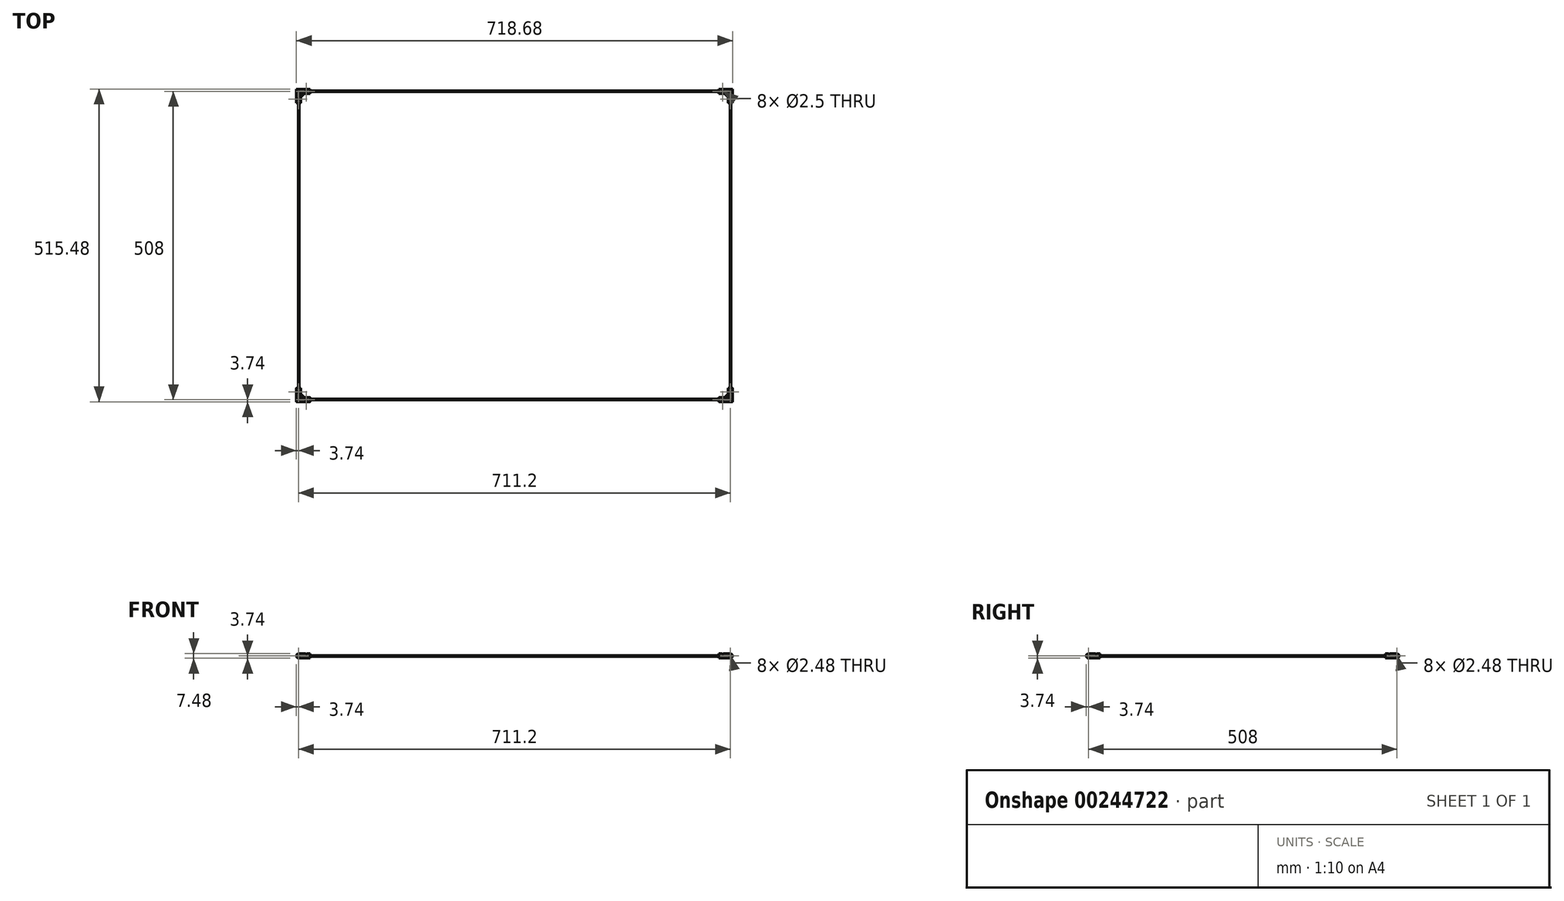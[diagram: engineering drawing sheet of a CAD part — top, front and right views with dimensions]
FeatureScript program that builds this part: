
annotation { "Feature Type Name" : "Feature", "Feature Type Description" : "" }
export const myFeature = defineFeature(function(context is Context, id is Id, definition is map)
    precondition{}
    {
        {
            var Q0;
            Q0=qCreatedBy(makeId("Right.planeOp"),FACE);
            var sketch = newSketch(context, id + "F0", { "sketchPlane" : qUnion([Q0])});
            skCircle(sketch, "E0", {"center": v(254, 0) * mm, "radius": 1 * mm});
            skSolve(sketch);
        }
        {
            var Q0;
            Q0 = qSketchRegion(id + "F0", true);
            extrude(context, id + "F1", {"entities" : qUnion([Q0]), "endBound" : BoundingType.SYMMETRIC, "depth" : 698.5 * mm});
        }
        {
            var Q0;
            Q0=qCreatedBy(makeId("Front.planeOp"),FACE);
            var sketch = newSketch(context, id + "F2", { "sketchPlane" : qUnion([Q0])});
            skCircle(sketch, "E1", {"center": v(355.6, 0) * mm, "radius": 1 * mm});
            skSolve(sketch);
        }
        {
            var Q0;
            Q0 = qSketchRegion(id + "F2", true);
            extrude(context, id + "F3", {"entities" : qUnion([Q0]), "endBound" : BoundingType.SYMMETRIC, "depth" : 495.3 * mm});
        }
        {
            var Q0;
            Q0=makeQuery(id+"F1.opExtrude","SWEPT_BODY",BODY,{"disambiguationData":[OSD([sQuery(id+"F0.wireOp",EDGE,"E0")])]});
            var Q1;
            Q1=qCreatedBy(makeId("Front.planeOp"),FACE);
            mirror(context, id + "F4", {"entities" : qUnion([Q0]), "mirrorPlane" : qUnion([Q1])});
        }
        {
            var Q0;
            Q0=makeQuery(id+"F3.opExtrude","SWEPT_BODY",BODY,{"disambiguationData":[OSD([sQuery(id+"F2.wireOp",EDGE,"E1")])]});
            var Q1;
            Q1=qCreatedBy(makeId("Right.planeOp"),FACE);
            mirror(context, id + "F5", {"entities" : qUnion([Q0]), "mirrorPlane" : qUnion([Q1])});
        }
        {
            var Q0;
            Q0=makeQuery(id+"F1.opExtrude","CAP_FACE",FACE,{"disambiguationData":[OSD([sQuery(id+"F0.wireOp",EDGE,"E0")])],"isStart":true});
            cPlane(context, id + "F6", {"entities" : qUnion([Q0]), "cplaneType" : CPlaneType.OFFSET, "offset" : 12.7 * mm, "oppositeDirection" : true, "width" : 150 * mm, "height" : 150 * mm});
        }
        {
            var Q0;
            Q0=makeQuery(id+"F5.opPattern","COPY",FACE,{"derivedFrom":makeQuery(id+"F3.opExtrude","CAP_FACE",FACE,{"disambiguationData":[OSD([sQuery(id+"F2.wireOp",EDGE,"E1")])],"isStart":true}),"instanceName":"1"});
            cPlane(context, id + "F7", {"entities" : qUnion([Q0]), "cplaneType" : CPlaneType.OFFSET, "offset" : 12.7 * mm, "oppositeDirection" : true, "width" : 150 * mm, "height" : 150 * mm});
        }
        {
            var Q0;
            Q0=qCreatedBy(id+"F6.planeOp",FACE);
            var sketch = newSketch(context, id + "F8", { "sketchPlane" : qUnion([Q0])});
            skCircle(sketch, "E2.0", {"center": v(-254, 0) * mm, "radius": 1 * mm, "construction": true});
            skCircle(sketch, "E3", {"center": v(-254, 0) * mm, "radius": 1.24 * mm});
            skCircle(sketch, "E4", {"center": v(-254, 0) * mm, "radius": 3.74 * mm});
            skSolve(sketch);
        }
        {
            var Q0;
            Q0=qCreatedBy(id+"F7.planeOp",FACE);
            var sketch = newSketch(context, id + "F9", { "sketchPlane" : qUnion([Q0])});
            skCircle(sketch, "E5.0", {"center": v(355.6, 0) * mm, "radius": 1 * mm, "construction": true});
            skCircle(sketch, "E6", {"center": v(355.6, 0) * mm, "radius": 1.24 * mm});
            skCircle(sketch, "E7", {"center": v(355.6, 0) * mm, "radius": 3.74 * mm});
            skSolve(sketch);
        }
        {
            var Q0;
            Q0=qCreatedBy(makeId("Top.planeOp"),FACE);
            var sketch = newSketch(context, id + "F10", { "sketchPlane" : qUnion([Q0])});
            skPoint(sketch, "E8.0", {"position": v(-355.6, 234.95) * mm});
            skPoint(sketch, "E9.0", {"position": v(-336.55, 254) * mm});
            skLineSegment(sketch, "E10", {"start": v(-355.6, 234.95) * mm, "end": v(-355.6, 254) * mm, "construction": true});
            skLineSegment(sketch, "E11", {"start": v(-336.55, 254) * mm, "end": v(-355.6, 254) * mm, "construction": true});
            skLineSegment(sketch, "E12", {"start": v(-355.6, 254) * mm, "end": v(-350.85, 249.25) * mm, "construction": true});
            skPoint(sketch, "E13", {"position": v(-342.9, 254) * mm});
            skPoint(sketch, "E14", {"position": v(-355.6, 241.3) * mm});
            skSolve(sketch);
        }
        {
            var Q0;
            Q0=sQuery(id+"F10.wireOp",EDGE,"E12");
            cPlane(context, id + "F11", {"entities" : qUnion([Q0]), "cplaneType" : CPlaneType.LINE_ANGLE, "offset" : 25 * mm, "angle" : 90 * degree, "width" : 150 * mm, "height" : 150 * mm});
        }
        {
            var Q0;
            Q0=makeQuery(id+"F9.imprint","IMPRINT",FACE,{"disambiguationData":[TD([[makeQuery(id+"F9.imprint","IMPRINT",EDGE,{"derivedFrom":sQuery(id+"F9.wireOp",EDGE,"E6")}),-1.0]])]});
            var Q1;
            Q1=qCreatedBy(id+"F11.planeOp",FACE);
            extrude(context, id + "F12", {"entities" : qUnion([Q0]), "endBound" : BoundingType.UP_TO_SURFACE, "endBoundEntityFace" : qUnion([Q1]), "depth" : 25 * mm});
        }
        {
            var Q0;
            Q0=makeQuery(id+"F8.imprint","IMPRINT",FACE,{"disambiguationData":[TD([[makeQuery(id+"F8.imprint","IMPRINT",EDGE,{"derivedFrom":sQuery(id+"F8.wireOp",EDGE,"E3")}),-1.0]])]});
            var Q1;
            Q1=makeQuery(id+"F12.opExtrude","CAP_FACE",FACE,{"disambiguationData":[OSD([sQuery(id+"F9.wireOp",EDGE,"E6"),sQuery(id+"F9.wireOp",EDGE,"E7")])],"isStart":false});
            extrude(context, id + "F13", {"entities" : qUnion([Q0]), "operationType" : NewBodyOperationType.ADD, "endBound" : BoundingType.UP_TO_SURFACE, "endBoundEntityFace" : qUnion([Q1]), "depth" : 25 * mm});
        }
        {
            var Q0;
            Q0=qCreatedBy(makeId("Top.planeOp"),FACE);
            var sketch = newSketch(context, id + "F14", { "sketchPlane" : qUnion([Q0])});
            skLineSegment(sketch, "E15", {"start": v(-336.55, 250.26) * mm, "end": v(-348.39, 250.26) * mm, "construction": true});
            skLineSegment(sketch, "E16", {"start": v(-351.86, 246.79) * mm, "end": v(-351.86, 234.95) * mm, "construction": true});
            skLineSegment(sketch, "E17", {"start": v(-351.86, 234.95) * mm, "end": v(-336.55, 250.26) * mm, "construction": true});
            skLineSegment(sketch, "E18", {"start": v(-352.96, 238.34) * mm, "end": v(-339.95, 251.35) * mm});
            skPoint(sketch, "E19.0", {"position": v(-336.55, 254) * mm});
            skPoint(sketch, "E20.0", {"position": v(-355.6, 234.95) * mm});
            skLineSegment(sketch, "E21", {"start": v(-336.55, 254) * mm, "end": v(-336.55, 250.26) * mm, "construction": true});
            skLineSegment(sketch, "E22", {"start": v(-355.6, 234.95) * mm, "end": v(-351.86, 234.95) * mm, "construction": true});
            skLineSegment(sketch, "E23", {"start": v(-352.96, 238.34) * mm, "end": v(-352.96, 251.35) * mm});
            skLineSegment(sketch, "E24", {"start": v(-352.96, 251.35) * mm, "end": v(-339.95, 251.35) * mm});
            skCircle(sketch, "E25", {"center": v(-350.46, 248.86) * mm, "radius": 1.4 * mm});
            skArc(sketch, "E26", {"start": v(-350.46, 246.36) * mm, "mid": v(-348.7, 247.09) * mm, "end": v(-347.96, 248.85) * mm});
            skLineSegment(sketch, "E27", {"start": v(-351.86, 246.79) * mm, "end": v(-351.86, 250.29) * mm});
            skArc(sketch, "E28", {"start": v(-350.2, 251.35) * mm, "mid": v(-350.46, 251.36) * mm, "end": v(-350.7, 251.35) * mm});
            skArc(sketch, "E29", {"start": v(-345.46, 251.35) * mm, "mid": v(-347.22, 250.62) * mm, "end": v(-347.96, 248.85) * mm});
            skArc(sketch, "E30", {"start": v(-350.46, 246.36) * mm, "mid": v(-352.23, 245.63) * mm, "end": v(-352.96, 243.86) * mm});
            skSolve(sketch);
        }
        {
            var Q0;
            Q0=qCreatedBy(makeId("Top.planeOp"),FACE);
            var sketch = newSketch(context, id + "F15", { "sketchPlane" : qUnion([Q0])});
            skPoint(sketch, "E31.0", {"position": v(-342.9, 254) * mm});
            skPoint(sketch, "E32.0", {"position": v(-355.6, 241.3) * mm});
            skCircle(sketch, "E33", {"center": v(-342.9, 254) * mm, "radius": 1.25 * mm});
            skCircle(sketch, "E34", {"center": v(-355.6, 241.3) * mm, "radius": 1.25 * mm});
            skSolve(sketch);
        }
        {
            var Q0;
            Q0 = qSketchRegion(id + "F15", true);
            extrude(context, id + "F16", {"entities" : qUnion([Q0]), "operationType" : NewBodyOperationType.REMOVE, "endBound" : BoundingType.SYMMETRIC, "oppositeDirection" : true, "depth" : 25 * mm});
        }
        {
            var Q0;
            Q0=makeQuery(id+"F14.imprint","IMPRINT",FACE,{"disambiguationData":[TD([[makeQuery(id+"F14.imprint","IMPRINT",EDGE,{"derivedFrom":sQuery(id+"F14.wireOp",EDGE,"E25")}),-1.0]])]});
            extrude(context, id + "F17", {"entities" : qUnion([Q0]), "operationType" : NewBodyOperationType.ADD, "endBound" : BoundingType.SYMMETRIC, "depth" : 5 * mm});
        }
        {
            var Q0;
            Q0=makeQuery(id+"F17.opExtrude","CAP_FACE",FACE,{"disambiguationData":[OSD([sQuery(id+"F14.wireOp",EDGE,"E23"),sQuery(id+"F14.wireOp",EDGE,"E24"),sQuery(id+"F14.wireOp",EDGE,"E25"),sQuery(id+"F14.wireOp",EDGE,"E26"),sQuery(id+"F14.wireOp",EDGE,"E29"),sQuery(id+"F14.wireOp",EDGE,"E30")])],"isStart":true});
            var sketch = newSketch(context, id + "F18", { "sketchPlane" : qUnion([Q0])});
            skPoint(sketch, "E35.0", {"position": v(-350.46, -248.86) * mm});
            skCircle(sketch, "E36", {"center": v(-350.46, -248.86) * mm, "radius": 1.75 * mm});
            skSolve(sketch);
        }
        {
            var Q0;
            Q0 = qSketchRegion(id + "F18", true);
            extrude(context, id + "F19", {"entities" : qUnion([Q0]), "operationType" : NewBodyOperationType.ADD, "oppositeDirection" : true, "depth" : 1 * mm});
        }
        {
            var Q0;
            Q0=makeQuery(id+"F12.opExtrude","SWEPT_BODY",BODY,{"disambiguationData":[OSD([sQuery(id+"F9.wireOp",EDGE,"E6"),sQuery(id+"F9.wireOp",EDGE,"E7")])]});
            var Q1;
            Q1=qCreatedBy(makeId("Right.planeOp"),FACE);
            mirror(context, id + "F20", {"entities" : qUnion([Q0]), "mirrorPlane" : qUnion([Q1])});
        }
        {
            var Q0;
            Q0=makeQuery(id+"F12.opExtrude","SWEPT_BODY",BODY,{"disambiguationData":[OSD([sQuery(id+"F9.wireOp",EDGE,"E6"),sQuery(id+"F9.wireOp",EDGE,"E7")])]});
            var Q1;
            Q1=makeQuery(id+"F20.opPattern","COPY",BODY,{"derivedFrom":makeQuery(id+"F12.opExtrude","SWEPT_BODY",BODY,{"disambiguationData":[OSD([sQuery(id+"F9.wireOp",EDGE,"E6"),sQuery(id+"F9.wireOp",EDGE,"E7")])]}),"instanceName":"1"});
            var Q2;
            Q2=qCreatedBy(makeId("Front.planeOp"),FACE);
            mirror(context, id + "F21", {"entities" : qUnion([Q0, Q1]), "mirrorPlane" : qUnion([Q2])});
        }
        {
            var Q0;
            Q0=sQuery(id+"F14.wireOp",EDGE,"E18");
            cPlane(context, id + "F22", {"entities" : qUnion([Q0]), "cplaneType" : CPlaneType.LINE_ANGLE, "offset" : 25 * mm, "angle" : 90 * degree, "width" : 150 * mm, "height" : 150 * mm});
        }
        {
            var Q0;
            Q0=qCreatedBy(id+"F22.planeOp",FACE);
            var sketch = newSketch(context, id + "F23", { "sketchPlane" : qUnion([Q0])});
            skPoint(sketch, "E37.0", {"position": v(-71.84, 0) * mm});
            skCircle(sketch, "E38", {"center": v(-71.84, 0) * mm, "radius": 1.25 * mm});
            skSolve(sketch);
        }
        {
            var Q0;
            Q0 = qSketchRegion(id + "F23", true);
            var Q1;
            Q1=makeQuery(id+"F17.opExtrude","SWEPT_FACE",FACE,{"disambiguationData":[OSD([sQuery(id+"F14.wireOp",EDGE,"E25")])]});
            extrude(context, id + "F24", {"entities" : qUnion([Q0]), "operationType" : NewBodyOperationType.REMOVE, "oppositeDirection" : true, "endBoundEntityFace" : qUnion([Q1]), "depth" : 6 * mm});
        }
    });
